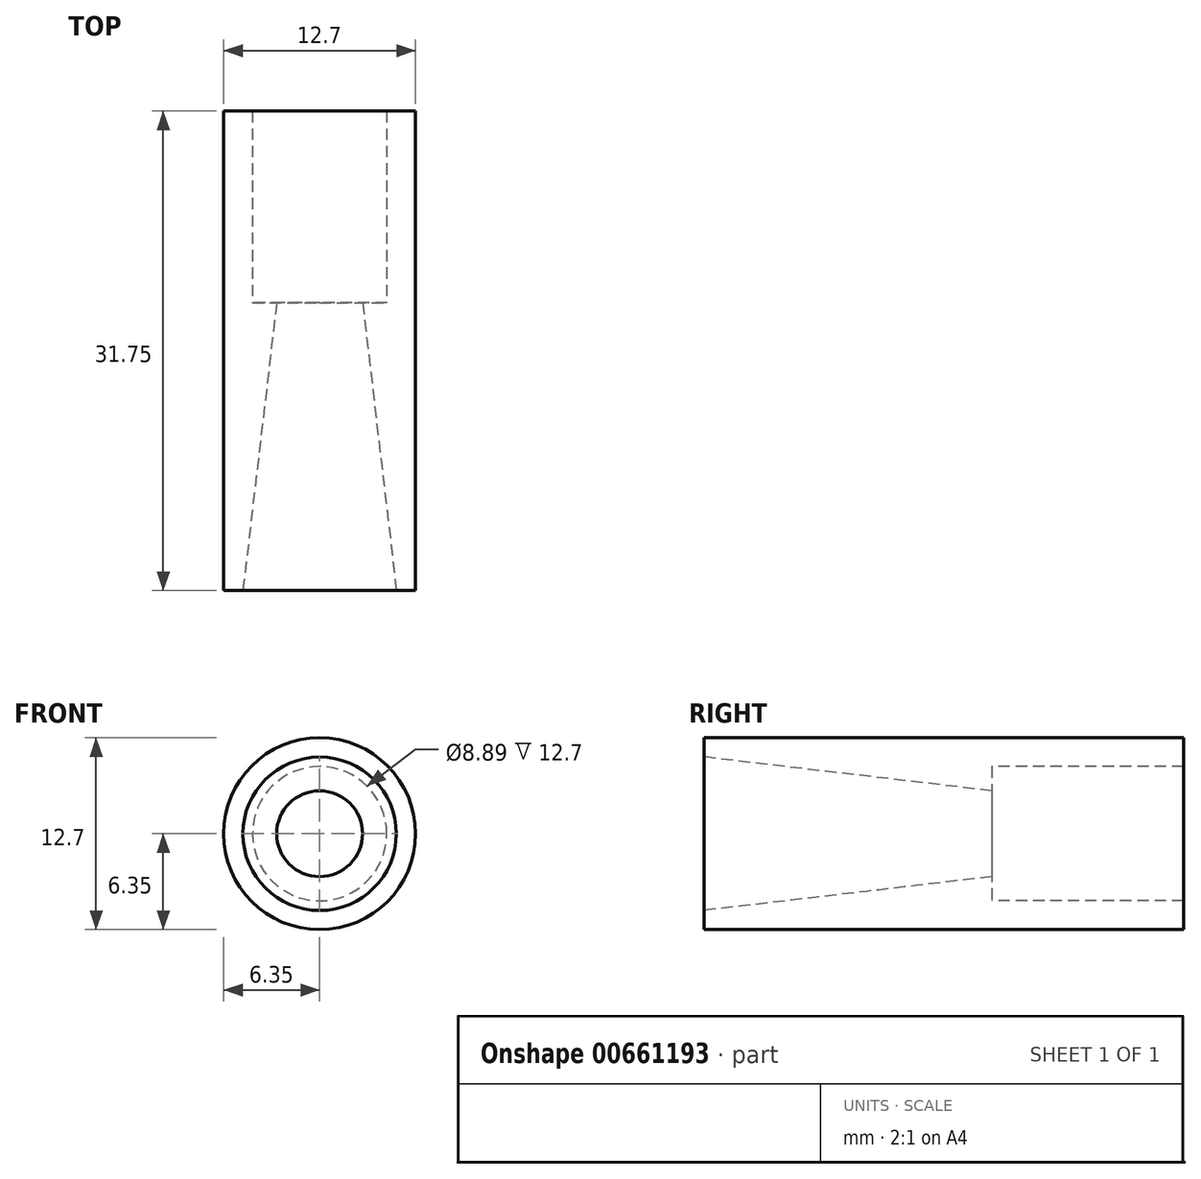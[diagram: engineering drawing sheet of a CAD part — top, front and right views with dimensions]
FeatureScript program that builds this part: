
annotation { "Feature Type Name" : "Feature", "Feature Type Description" : "" }
export const myFeature = defineFeature(function(context is Context, id is Id, definition is map)
    precondition{}
    {
        {
            var Q0;
            Q0=qCreatedBy(makeId("Front.planeOp"),FACE);
            var sketch = newSketch(context, id + "F0", { "sketchPlane" : qUnion([Q0])});
            skCircle(sketch, "E0", {"center": v(0, 0) * mm, "radius": 6.35 * mm});
            skSolve(sketch);
        }
        {
            var Q0;
            Q0=makeQuery(id+"F0.imprint","IMPRINT",FACE,{"disambiguationData":[TD([[makeQuery(id+"F0.imprint","IMPRINT",EDGE,{"derivedFrom":sQuery(id+"F0.wireOp",EDGE,"E0")}),1.0]])]});
            var sketch = newSketch(context, id + "F1", { "sketchPlane" : qUnion([Q0])});
            skCircle(sketch, "E1", {"center": v(0, 0) * mm, "radius": 5.08 * mm});
            skSolve(sketch);
        }
        {
            var Q0;
            Q0=qCreatedBy(makeId("Top.planeOp"),FACE);
            var sketch = newSketch(context, id + "F2", { "sketchPlane" : qUnion([Q0])});
            skLineSegment(sketch, "E2", {"start": v(0, 0) * mm, "end": v(0, 19.05) * mm});
            skSolve(sketch);
        }
        {
            var Q0;
            Q0=sQuery(id+"F2.wireOp",EDGE,"E2");
            var Q1;
            Q1=sQuery(id+"F2.wireOp",VERTEX,"E2.end");
            cPlane(context, id + "F3", {"entities" : qUnion([Q0, Q1]), "cplaneType" : CPlaneType.LINE_POINT, "offset" : 25.4 * mm, "width" : 152.4 * mm, "height" : 152.4 * mm});
        }
        {
            var Q0;
            Q0=qCreatedBy(id+"F3.planeOp",FACE);
            var sketch = newSketch(context, id + "F4", { "sketchPlane" : qUnion([Q0])});
            skCircle(sketch, "E3", {"center": v(0, 0) * mm, "radius": 2.84 * mm});
            skSolve(sketch);
        }
        {
            var Q0;
            Q0=makeQuery(id+"F0.imprint","IMPRINT",FACE,{"disambiguationData":[TD([[makeQuery(id+"F0.imprint","IMPRINT",EDGE,{"derivedFrom":sQuery(id+"F0.wireOp",EDGE,"E0")}),1.0]])]});
            extrude(context, id + "F5", {"entities" : qUnion([Q0]), "oppositeDirection" : true, "depth" : 19.05 * mm, "offsetDistance" : 25.4 * mm});
        }
        {
            var Q1;
            Q1=makeQuery(id+"F1.imprint","IMPRINT",FACE,{"disambiguationData":[TD([[makeQuery(id+"F1.imprint","IMPRINT",EDGE,{"derivedFrom":sQuery(id+"F1.wireOp",EDGE,"E1")}),1.0]])]});
            var Q2;
            Q2=makeQuery(id+"F4.imprint","IMPRINT",FACE,{"disambiguationData":[TD([[makeQuery(id+"F4.imprint","IMPRINT",EDGE,{"derivedFrom":sQuery(id+"F4.wireOp",EDGE,"E3")}),1.0]])]});
            loft(context, id + "F6", {"operationType" : NewBodyOperationType.REMOVE, "sheetProfilesArray" : [{ "sheetProfileEntities" : qUnion([Q1]) }, { "sheetProfileEntities" : qUnion([Q2]) }]});
        }
        {
            var Q0;
            Q0=makeQuery(id+"F5.opExtrude","CAP_FACE",FACE,{"disambiguationData":[OSD([sQuery(id+"F0.wireOp",EDGE,"E0")])],"isStart":false});
            var sketch = newSketch(context, id + "F7", { "sketchPlane" : qUnion([Q0])});
            skCircle(sketch, "E4", {"center": v(0, 0) * mm, "radius": 4.45 * mm});
            skSolve(sketch);
        }
        {
            var Q0;
            Q0=makeQuery(id+"F7.imprint","IMPRINT",FACE,{"disambiguationData":[TD([[makeQuery(id+"F7.imprint","IMPRINT",EDGE,{"derivedFrom":sQuery(id+"F7.wireOp",EDGE,"E4")}),-1.0]])]});
            extrude(context, id + "F8", {"entities" : qUnion([Q0]), "operationType" : NewBodyOperationType.ADD, "depth" : 12.7 * mm, "offsetDistance" : 25.4 * mm});
        }
    });
